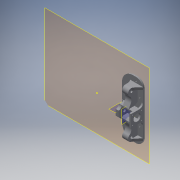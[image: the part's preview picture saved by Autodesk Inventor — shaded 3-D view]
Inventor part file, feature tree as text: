
AUTODESK INVENTOR PART (.ipt)
format: ipt  version: 2016 (Build 200138000, 138)  size: 444,928 bytes
history: native  units: in
note: dims shown in document units (in); Inventor stores cm internally (conversion verified against a paired STEP export)
features: sketch x14, extrude x12, projected_geometry x8, fillet x6, plane x3, chamfer x2, reference x1
ambient origin geometry x8: Origin, YZ Plane, XZ Plane, XY Plane, X Axis, Y Axis, Z Axis, Center Point
bodies: Solid1 (feature_tree)
feature tree (46):
  plane  "Work Plane1"
  extrude  "Extrusion1"  Depth=0.2in TaperAngle=0.0deg
  extrude  "Extrusion2"  TaperAngle=90.0deg  [1 undecoded]
  extrude  "Extrusion3"  Depth=1.7in
  extrude  "Extrusion4"  Depth=0.6102in
  extrude  "Extrusion5"  Depth=0.1181in
  extrude  "Extrusion6"  Depth=0.2362in TaperAngle=0.0deg
  extrude  "Extrusion7"  Depth=0.8in
  plane  "Work Plane2"
  extrude  "Extrusion8"  Depth=1.4961in TaperAngle=0.0deg
  extrude  "Extrusion9"  Depth=0.3937in TaperAngle=0.0deg
  fillet  "Fillet1"  Radius=0.45in
  fillet  "Fillet2"  Radius=0.45in
  fillet  "Fillet3"  Radius=0.45in
  sketch  "Sketch10"  dims[d33=0.45in d34=0.8312in d35=0.0in]
  sketch  "Sketch11"  dims[d36=0.3937in d37=0.0787in d38=0.0in]
  chamfer  "Chamfer1"  Distance=0.8312in
  chamfer  "Chamfer2"  Distance=0.0787in
  extrude  "Extrusion10"  Depth=0.9375in
  extrude  "Extrusion11"  Depth=2.7559in
  plane  "Work Plane3"
  extrude  "Extrusion12"  Depth=0.5in
  fillet  "Fillet4"  Radius=0.315in
  fillet  "Fillet5"  Radius=1.0in
  fillet  "Fillet6"  Radius=1.0in
  sketch  "Sketch1"  dims[d0=8.0in d1=0.2in d2=0.0in]
  reference  "Reference1"
  sketch  "Sketch2"  dims[d3=0.85in d4=90.0deg]
  projected_geometry  "Projected Loop1"
  sketch  "Sketch3"  dims[d5=1.7in d6=1.7in]
  projected_geometry  "Projected Loop2"
  sketch  "Sketch4"  dims[d7=0.9843in d8=0.6102in]
  projected_geometry  "Projected Loop3"
  sketch  "Sketch5"  dims[d9=0.6102in d10=0.1181in]
  projected_geometry  "Projected Loop4"
  sketch  "Sketch6"  dims[d11=0.7874in d13=1.2205in d14=0.7874in d16=1.2205in d19=0.2362in d20=0.0in]
  projected_geometry  "Projected Loop5"
  sketch  "Sketch7"  dims[d21=0.8in d22=0.8in]
  projected_geometry  "Projected Loop6"
  sketch  "Sketch8"  dims[d23=0.8in d24=1.4961in d25=0.0in]
  sketch  "Sketch9"  dims[d26=0.8661in d27=0.3937in d28=0.0in d30=0.45in d31=0.45in d32=0.45in]
  sketch  "Sketch12"  dims[d39=0.4537in d40=0.0in d41=0.9375in]
  projected_geometry  "Projected Loop7"
  sketch  "Sketch13"  dims[d42=0.8287in d43=0.0in d45=2.7559in]
  projected_geometry  "Projected Loop8"
  sketch  "Sketch14"  dims[d46=0.315in d47=2.7559in d48=0.315in d49=1.0in d50=1.0in d51=0.8287in d52=0.0in d53=1.5625in d54=1.0in d55=0.8125in d56=0.1875in d57=0.125in d58=45.0deg d59=0.25in d60=0.125in d61=45.0deg d62=0.3287in d63=0.0in d64=0.3287in d65=0.0in d66=0.6412in d67=0.0in d68=0.8125in d69=0.8125in d70=0.5in]
note: 1 required parameter value undecoded (feature->parameter linkage not recoverable at this tier; creation-order binding heuristic only, values carry confidence <= 0.55)
